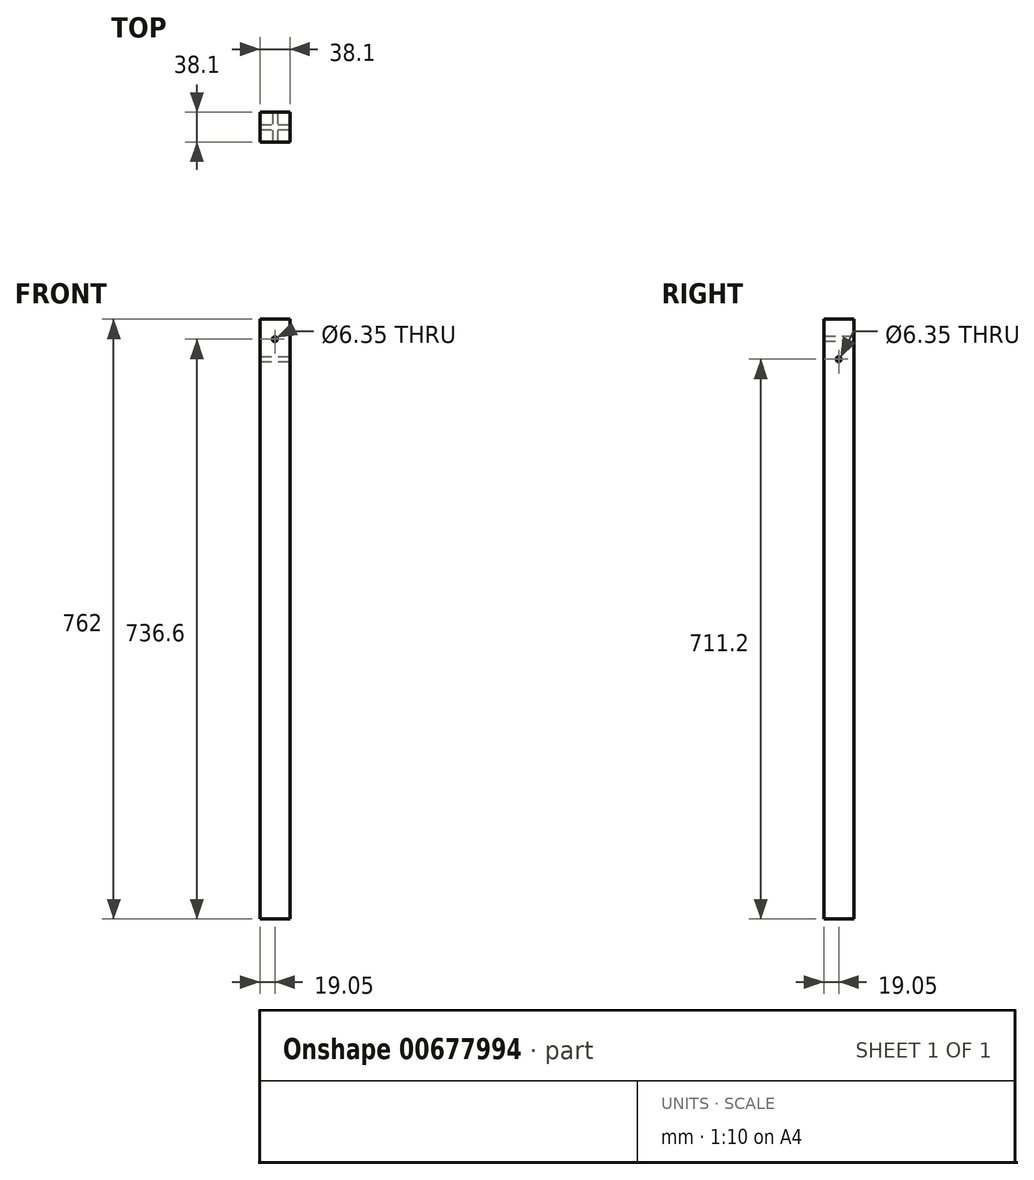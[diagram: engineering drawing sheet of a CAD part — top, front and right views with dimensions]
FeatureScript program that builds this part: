
annotation { "Feature Type Name" : "Feature", "Feature Type Description" : "" }
export const myFeature = defineFeature(function(context is Context, id is Id, definition is map)
    precondition{}
    {
        {
            var Q0;
            Q0=qCreatedBy(makeId("Top.planeOp"),FACE);
            var sketch = newSketch(context, id + "F0", { "sketchPlane" : qUnion([Q0])});
            skLineSegment(sketch, "E0.bottom", {"start": v(19.05, 19.05) * mm, "end": v(-19.05, 19.05) * mm});
            skLineSegment(sketch, "E0.top", {"start": v(19.05, -19.05) * mm, "end": v(-19.05, -19.05) * mm});
            skLineSegment(sketch, "E0.left", {"start": v(19.05, 19.05) * mm, "end": v(19.05, -19.05) * mm});
            skLineSegment(sketch, "E0.right", {"start": v(-19.05, 19.05) * mm, "end": v(-19.05, -19.05) * mm});
            skPoint(sketch, "E0.middle", {"position": v(0, 0) * mm});
            skSolve(sketch);
        }
        {
            var Q0;
            Q0 = qSketchRegion(id + "F0", true);
            extrude(context, id + "F1", {"entities" : qUnion([Q0]), "oppositeDirection" : true, "depth" : 762 * mm, "offsetDistance" : 25.4 * mm});
        }
        {
            var Q0;
            Q0=makeQuery(id+"F1.opExtrude","SWEPT_FACE",FACE,{"disambiguationData":[OSD([sQuery(id+"F0.wireOp",EDGE,"E0.top")])]});
            var sketch = newSketch(context, id + "F2", { "sketchPlane" : qUnion([Q0])});
            skCircle(sketch, "E1", {"center": v(0, -25.4) * mm, "radius": 3.18 * mm});
            skSolve(sketch);
        }
        {
            var Q0;
            Q0 = qSketchRegion(id + "F2", true);
            extrude(context, id + "F3", {"entities" : qUnion([Q0]), "operationType" : NewBodyOperationType.REMOVE, "endBound" : BoundingType.THROUGH_ALL, "oppositeDirection" : true, "depth" : 25.4 * mm, "offsetDistance" : 25.4 * mm});
        }
        {
            var Q0;
            Q0=makeQuery(id+"F1.opExtrude","SWEPT_FACE",FACE,{"disambiguationData":[OSD([sQuery(id+"F0.wireOp",EDGE,"E0.left")])]});
            var sketch = newSketch(context, id + "F4", { "sketchPlane" : qUnion([Q0])});
            skCircle(sketch, "E2", {"center": v(0, -50.8) * mm, "radius": 3.18 * mm});
            skSolve(sketch);
        }
        {
            var Q0;
            Q0 = qSketchRegion(id + "F4", true);
            extrude(context, id + "F5", {"entities" : qUnion([Q0]), "operationType" : NewBodyOperationType.REMOVE, "endBound" : BoundingType.THROUGH_ALL, "oppositeDirection" : true, "depth" : 25.4 * mm, "offsetDistance" : 25.4 * mm});
        }
    });
